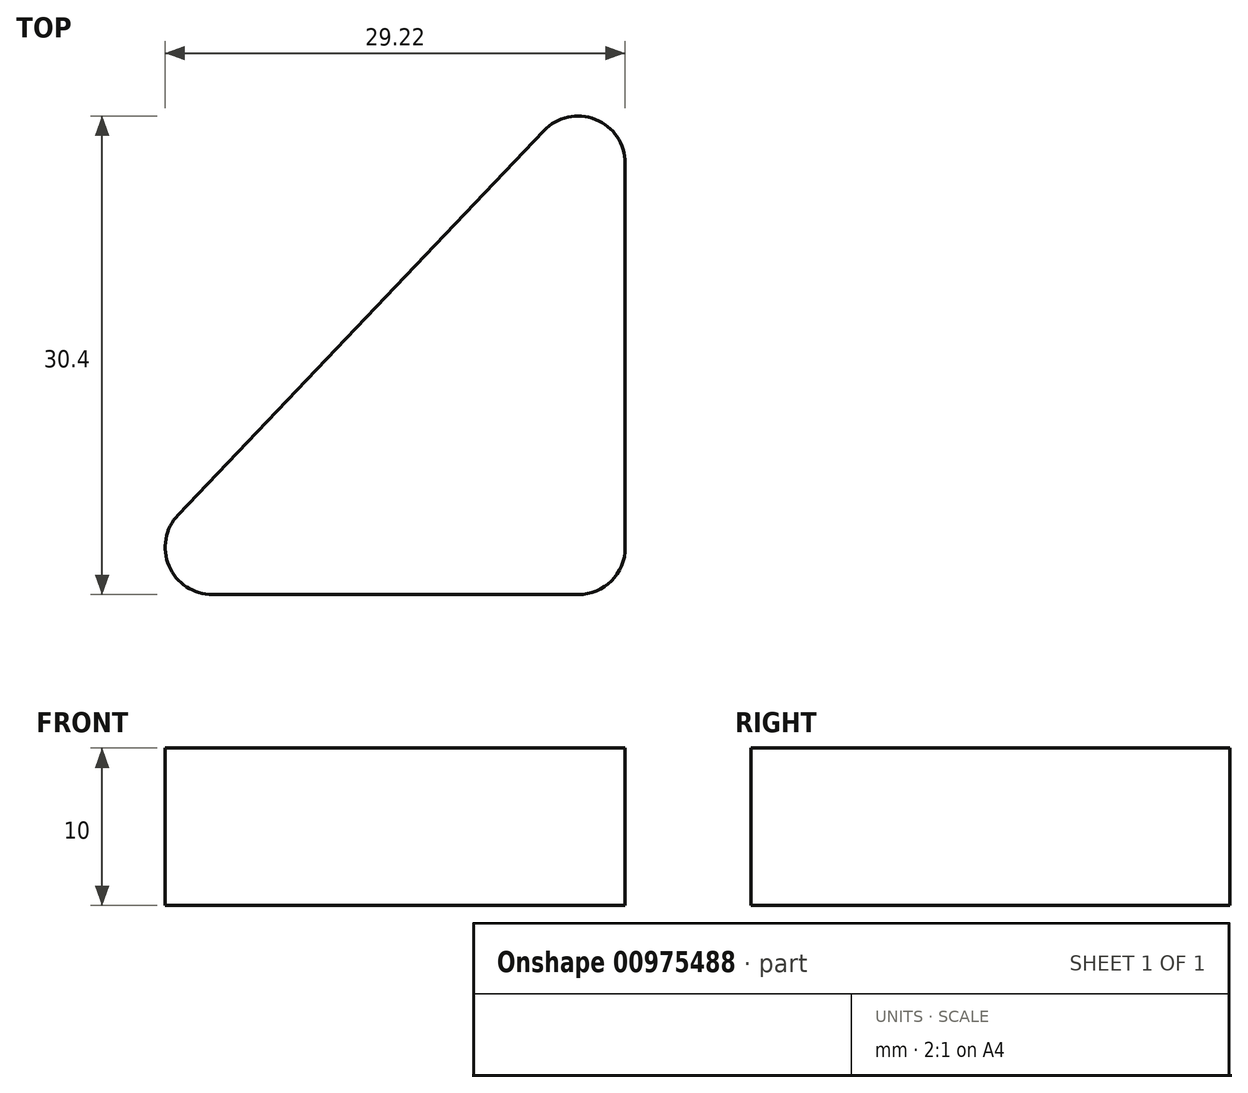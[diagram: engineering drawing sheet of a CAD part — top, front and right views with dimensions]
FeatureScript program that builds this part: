
annotation { "Feature Type Name" : "Feature", "Feature Type Description" : "" }
export const myFeature = defineFeature(function(context is Context, id is Id, definition is map)
    precondition{}
    {
        {
            var Q0;
            Q0=qCreatedBy(makeId("Top.planeOp"),FACE);
            var sketch = newSketch(context, id + "F0", { "sketchPlane" : qUnion([Q0])});
            skLineSegment(sketch, "E0", {"start": v(0, 34.9) * mm, "end": v(-33.21, 0) * mm});
            skLineSegment(sketch, "E1", {"start": v(-33.21, 0) * mm, "end": v(0, 0) * mm});
            skLineSegment(sketch, "E2", {"start": v(0, 0) * mm, "end": v(0, 34.9) * mm});
            skSolve(sketch);
        }
        {
            var Q0;
            Q0=makeQuery(id+"F0.imprint","IMPRINT",FACE,{"disambiguationData":[TD([[makeQuery(id+"F0.imprint","IMPRINT",EDGE,{"derivedFrom":sQuery(id+"F0.wireOp",EDGE,"E0")}),1.0]])]});
            extrude(context, id + "F1", {"entities" : qUnion([Q0]), "depth" : 10 * mm, "offsetDistance" : 25 * mm});
        }
        {
            var Q0;
            Q0=makeQuery(id+"F1.opExtrude","SWEPT_EDGE",EDGE,{"disambiguationData":[OSD([sQuery(id+"F0.wireOp",EDGE,"E1"),sQuery(id+"F0.wireOp",EDGE,"E2")])]});
            var Q1;
            Q1=makeQuery(id+"F1.opExtrude","SWEPT_EDGE",EDGE,{"disambiguationData":[OSD([sQuery(id+"F0.wireOp",EDGE,"E0"),sQuery(id+"F0.wireOp",EDGE,"E1")])]});
            var Q2;
            Q2=makeQuery(id+"F1.opExtrude","SWEPT_EDGE",EDGE,{"disambiguationData":[OSD([sQuery(id+"F0.wireOp",EDGE,"E0"),sQuery(id+"F0.wireOp",EDGE,"E2")])]});
            fillet(context, id + "F2", {"entities" : qUnion([Q0, Q1, Q2]), "radius" : 3 * mm, "tangentPropagation" : true, "allowEdgeOverflow" : false});
        }
    });
